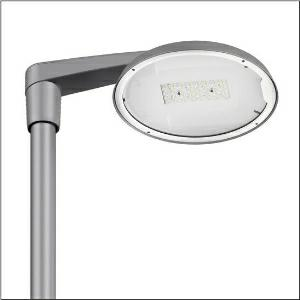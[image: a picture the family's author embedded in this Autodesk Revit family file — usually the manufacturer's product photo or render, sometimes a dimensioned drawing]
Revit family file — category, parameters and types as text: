
# Revit family: dl_r__50_iq_mini___st0_5a_5xa248b41f08ge_47f6
name_source: partatom
category: Lighting Fixtures
units: mm (PartAtom-declared; Revit-internal decimal feet)

## family parameters
Cut with Voids When Loaded = No
Host = Face
Light Source = No
Part Type = Normal
Room Calculation Point = No
Round Connector Dimension = Use Diameter
Shared = No

## types (1)
- --- (1 x LED, 5190 lm, 31.2 W, 4000K)
    Apparent Load = 31 VA
    CIE Flux Codes = 41 75 97 100 100
    Color Rendering = 70
    Color Temperature = 4000K
    Default Elevation = 1800 mm
    Description = DL® 50 iQ mini, mast luminaire, primary light control with lens, of PMMA, primary optical cover: cover, of toughened safety glass, transparent, light distribution: ST0.5a, light emission: direct distribution, primary light characteristic: asymmetric, installation type: side-entry, post-top, LED, High Power LED, rated luminous flux: 5.190lm, luminous efficacy: 166lm/W, light colour: 740, colour temperature: 4000K, control gear: iQ Street-Remote, control: optimised constant luminous flux control (CLO 2.0), Desk-Remote (wireless, voltage-free reading and setting of iQ features in the workshop via application-optimized NFC function/RFID function), Light-Fading, Smart-Wire, Night-Set, Lumen-Switch, Temp-Guard, Auto-Match, Street-Remote, mains connection: 230..240V, AC, 50/60Hz, connection cable pre-assembled, cable length: 6,5m, start of lifetime: 31W, end of service life: 32W, reduction: 15W, luminaire housing, of diecast aluminium, powder-coated, Siteco® metallic grey (DB 702S), inclination adjustable: 0°, 5°, 10° (post-top) | 0°, -5°, -10°, -15° (side-entry), please order mast post-top element or mast side-entry element separately, diameter: 500mm, height: 115mm, post-top: for spigot size d x l = 76 x 100mm; with reducer (optional accessory) 60 x 100mm | side-entry: for spigot size d x l = 60 x 100mm; with reducer (optional accessory) 42 x 100mm, mounting height: 4..6m, protection rating (complete): IP66, insulation class (complete): insulation class II (safety insulation), certification: CE, ENEC, ENEC+, VDE, impact resistance: IK08, permissible operating ambient temperature for outdoor applications: -25..+40°C, standard-compliant lighting for roads and squares, packaging unit: 1 piece

Light Distribution: ST0.5a
    Height = 115 mm
    Lamp = 1 x LED
    Lamp Light Flux = 5190 lm
    Lamp Power = 31.2 W
    Lamp count = 1
    Length = 500 mm
    Luminous efficacy = 166 lm/W
    Manufacturer = Siteco
    ModVariant = No
    Model = 5XA248B41F08GE
    Number of Poles = 1
    OnlyDefault = Yes
    Power Factor = 1
    Product Name = DL® 50 iQ mini | ST0.5a
    Product group = mast luminaire | pylon top
    ProductGroupID = 6100
    Protection Class = Protection class II
    Protection Degree = IP 66
    RLX_Detail_Level = 1
    RLX_Emergency_Light_Flux = 0 lm
    RLX_Emergency_Type = 0
    RLX_Emergency_Type_DB = No
    RlxData = <blob elided: 126981 chars, md5=329a3481>
    Socket = socket
    Standby Power = 0 W
    System Light Flux = 5190 lm
    System Power = 31 W
    Type Comments = factory setting: luminous flux: 100 % | dim-lin: 254 | 325 mA
    Type Image = l_1251794.jpg
    URL = http://relux.com
    VarID = @adj_164741
    Voltage = 0 V
    Weight = 0.00 kg
    Width = 0 mm  [stored 0 ft]

note: [stored X ft] marks values corroborated as IEEE doubles in the binary element streams (Revit-internal decimal feet)

## geometry (parser evidence)
native form markers: Blend x4, Sweep x11
no freeform markers — native parametric forms only
